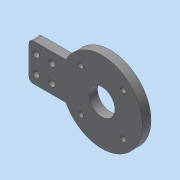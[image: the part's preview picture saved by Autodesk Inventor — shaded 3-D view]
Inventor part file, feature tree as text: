
AUTODESK INVENTOR PART (.ipt)
format: ipt  version: 2017 (Build 210142000, 142)  size: 134,144 bytes
history: native  units: in
note: dims shown in document units (in); Inventor stores cm internally (conversion verified against a paired STEP export)
features: other x8, extrude x2, sketch x1
ambient origin geometry x8: Origin, YZ Plane, XZ Plane, XY Plane, X Axis, Y Axis, Z Axis, Center Point
bodies: Solid1 (feature_tree)
feature tree (11):
  sketch  "Sketch1"  dims[d0=2.3228in d2=0.125in d9=0.816in d10=0.19in d13=0.7874in d15=0.45in d16=0.7874in d18=0.5in d21=0.1575in d23=0.1575in d24=0.1575in d25=0.1575in d26=45.0deg d27=0.25in d28=0.0in d29=1.0in d30=0.0in d31=1.0in d32=0.0in d33=1.0in d34=0.0in d35=1.0in d36=0.0in d37=1.0in d38=0.0in d39=1.0in d40=0.0in d41=1.0in d42=0.0in d43=1.0in d44=0.0in d45=0.75in d46=1.0in d47=0.0in d48=1.2205in d49=1.2205in d50=1.2205in d51=0.2in d52=1.06in d53=0.6102in]
  extrude  "plate"  Depth=0.125in
  extrude  "motor hole"  Depth=0.25in
  other  "platethread1"
  other  "platethread2"
  other  "platethread3"
  other  "platethread4"
  other  "motorthread1"
  other  "motorthread2"
  other  "motorthread3"
  other  "motorthread4"
